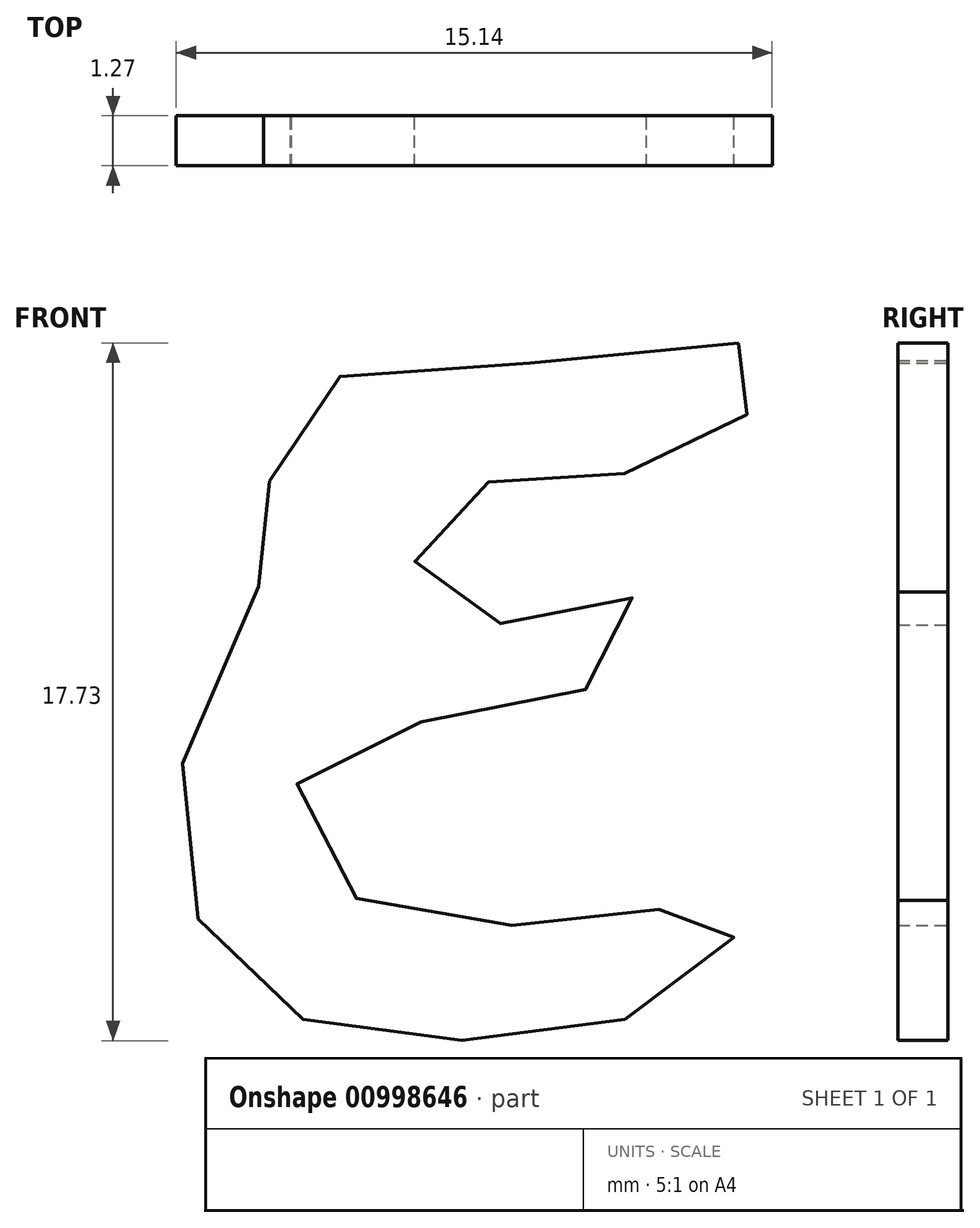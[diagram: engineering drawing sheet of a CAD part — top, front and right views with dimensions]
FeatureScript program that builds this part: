
annotation { "Feature Type Name" : "Feature", "Feature Type Description" : "" }
export const myFeature = defineFeature(function(context is Context, id is Id, definition is map)
    precondition{}
    {
        {
            var Q0;
            Q0=qCreatedBy(makeId("Front.planeOp"),FACE);
            var sketch = newSketch(context, id + "F0", { "sketchPlane" : qUnion([Q0])});
            skFitSpline(sketch, "E0", {"points": [v(-47.24, 22.97) * mm, v(-49.1, 22.78) * mm, v(-50.85, 22.6) * mm, v(-52.7, 22.46) * mm, v(-54.47, 22.52) * mm, v(-55.92, 22.46) * mm, v(-57.23, 22.17) * mm, v(-58.3, 21.53) * mm, v(-58.97, 20.74) * mm, v(-59.28, 20.08) * mm, v(-59.26, 19.68) * mm, v(-59.1, 19.4) * mm, v(-58.93, 19.24) * mm, v(-58.76, 19.07) * mm, v(-58.63, 18.78) * mm, v(-58.66, 18.35) * mm, v(-59.13, 17.31) * mm, v(-59.72, 16.2) * mm, v(-60.3, 14.91) * mm, v(-61, 13.4) * mm, v(-61.47, 11.75) * mm, v(-61.5, 10.6) * mm, v(-61.37, 9.66) * mm, v(-61.16, 8.8) * mm, v(-60.75, 7.95) * mm, v(-60.26, 7.24) * mm, v(-59.7, 6.62) * mm, v(-59.03, 6.11) * mm, v(-57.89, 5.65) * mm, v(-56.9, 5.43) * mm, v(-55.73, 5.29) * mm, v(-54.7, 5.26) * mm, v(-53.61, 5.24) * mm, v(-52.33, 5.34) * mm, v(-51.43, 5.48) * mm, v(-50.3, 5.72) * mm, v(-49.27, 6.1) * mm, v(-48.35, 6.6) * mm, v(-47.74, 7.17) * mm, v(-47.42, 7.65) * mm, v(-47.34, 8.01) * mm, v(-47.44, 8.4) * mm, v(-47.62, 8.6) * mm, v(-47.82, 8.73) * mm, v(-48.06, 8.8) * mm, v(-48.5, 8.75) * mm, v(-49.24, 8.58) * mm, v(-49.94, 8.44) * mm, v(-50.7, 8.35) * mm, v(-51.63, 8.26) * mm, v(-52.8, 8.18) * mm, v(-53.84, 8.18) * mm, v(-54.87, 8.24) * mm, v(-55.9, 8.46) * mm, v(-56.93, 8.84) * mm, v(-57.83, 9.4) * mm, v(-58.28, 10.02) * mm, v(-58.56, 10.66) * mm, v(-58.52, 11.53) * mm, v(-58.24, 12.23) * mm, v(-57.75, 12.82) * mm, v(-56.92, 13.12) * mm, v(-55.78, 13.29) * mm, v(-54.62, 13.4) * mm, v(-53.33, 13.56) * mm, v(-52.21, 13.83) * mm, v(-51.18, 14.13) * mm, v(-50.3, 14.58) * mm, v(-49.86, 15) * mm, v(-49.6, 15.59) * mm, v(-49.62, 16.08) * mm, v(-49.94, 16.5) * mm, v(-50.45, 16.63) * mm, v(-51.11, 16.48) * mm, v(-51.86, 16.2) * mm, v(-52.77, 15.94) * mm, v(-53.75, 15.8) * mm, v(-54.44, 15.94) * mm, v(-54.95, 16.21) * mm, v(-55.32, 16.63) * mm, v(-55.46, 17.14) * mm, v(-55.4, 17.68) * mm, v(-55.17, 18.24) * mm, v(-54.9, 18.63) * mm, v(-54.52, 19) * mm, v(-54.1, 19.27) * mm, v(-53.46, 19.46) * mm, v(-52.57, 19.57) * mm, v(-51.73, 19.58) * mm, v(-50.9, 19.6) * mm, v(-50.34, 19.63) * mm, v(-49.69, 19.72) * mm, v(-49.02, 19.92) * mm, v(-48.1, 20.33) * mm, v(-47.47, 20.78) * mm, v(-46.9, 21.26) * mm, v(-46.49, 21.74) * mm, v(-46.38, 22.1) * mm, v(-46.4, 22.4) * mm, v(-46.55, 22.66) * mm, v(-46.82, 22.88) * mm, v(-47.24, 22.97) * mm]});
            skLineSegment(sketch, "E1.bottom", {"start": v(-120.44, 77.9) * mm, "end": v(12.9, 77.9) * mm});
            skLineSegment(sketch, "E1.top", {"start": v(-120.44, -131.65) * mm, "end": v(12.9, -131.65) * mm});
            skLineSegment(sketch, "E1.left", {"start": v(-120.44, 77.9) * mm, "end": v(-120.44, -131.65) * mm});
            skLineSegment(sketch, "E1.right", {"start": v(12.9, 77.9) * mm, "end": v(12.9, -131.65) * mm});
            skLineSegment(sketch, "E2", {"start": v(-53.77, 77.9) * mm, "end": v(-53.77, -131.65) * mm, "construction": true});
            skLineSegment(sketch, "E3", {"start": v(-120.44, 14.4) * mm, "end": v(12.9, 14.4) * mm, "construction": true});
            skLineSegment(sketch, "E4", {"start": v(-61.7, 14.4) * mm, "end": v(-63.46, 14.4) * mm, "construction": true});
            skLineSegment(sketch, "E5", {"start": v(-53.77, 23.92) * mm, "end": v(-53.77, 28.89) * mm, "construction": true});
            skLineSegment(sketch, "E6", {"start": v(-53.77, 28.89) * mm, "end": v(-53.93, 28.89) * mm, "construction": true});
            skPoint(sketch, "E7.orphan", {"position": v(-61.7, 23.92) * mm});
            skPoint(sketch, "E8.orphan", {"position": v(-61.7, 4.87) * mm});
            skPoint(sketch, "E9.right.start.orphan", {"position": v(-45.83, 23.92) * mm});
            skFitSpline(sketch, "E10.0", {"points": [v(-46.96, 23) * mm, v(-47.22, 23.02) * mm, v(-47.62, 23) * mm, v(-48.11, 22.95) * mm, v(-48.65, 22.88) * mm, v(-49.36, 22.8) * mm, v(-49.98, 22.74) * mm, v(-50.57, 22.68) * mm, v(-51.18, 22.62) * mm, v(-51.82, 22.55) * mm, v(-52.48, 22.51) * mm, v(-53.12, 22.5) * mm, v(-53.92, 22.55) * mm, v(-54.82, 22.58) * mm, v(-55.67, 22.54) * mm, v(-56.5, 22.44) * mm, v(-57.3, 22.23) * mm, v(-57.9, 21.9) * mm, v(-58.32, 21.59) * mm, v(-58.69, 21.24) * mm, v(-58.97, 20.85) * mm, v(-59.2, 20.46) * mm, v(-59.32, 20.18) * mm, v(-59.36, 19.92) * mm, v(-59.33, 19.7) * mm, v(-59.24, 19.49) * mm, v(-59.11, 19.32) * mm, v(-58.97, 19.22) * mm, v(-58.85, 19.11) * mm, v(-58.75, 18.98) * mm, v(-58.68, 18.8) * mm, v(-58.65, 18.6) * mm, v(-58.7, 18.37) * mm, v(-58.81, 18.05) * mm, v(-58.98, 17.7) * mm, v(-59.18, 17.33) * mm, v(-59.37, 16.98) * mm, v(-59.56, 16.64) * mm, v(-59.8, 16.17) * mm, v(-60.02, 15.66) * mm, v(-60.25, 15.14) * mm, v(-60.5, 14.61) * mm, v(-60.77, 14.07) * mm, v(-61.02, 13.5) * mm, v(-61.25, 12.9) * mm, v(-61.43, 12.28) * mm, v(-61.53, 11.7) * mm, v(-61.58, 11.16) * mm, v(-61.56, 10.56) * mm, v(-61.48, 9.98) * mm, v(-61.4, 9.54) * mm, v(-61.33, 9.2) * mm, v(-61.25, 8.88) * mm, v(-61.09, 8.45) * mm, v(-60.81, 7.93) * mm, v(-60.51, 7.47) * mm, v(-60.24, 7.13) * mm, v(-60.02, 6.88) * mm, v(-59.8, 6.65) * mm, v(-59.56, 6.43) * mm, v(-59.31, 6.23) * mm, v(-59.02, 6.04) * mm, v(-58.66, 5.87) * mm, v(-58.28, 5.72) * mm, v(-57.9, 5.6) * mm, v(-57.55, 5.5) * mm, v(-57.21, 5.43) * mm, v(-56.74, 5.35) * mm, v(-56.22, 5.28) * mm, v(-55.7, 5.23) * mm, v(-55.21, 5.2) * mm, v(-54.75, 5.2) * mm, v(-54.27, 5.2) * mm, v(-53.9, 5.19) * mm, v(-53.51, 5.2) * mm, v(-52.96, 5.22) * mm, v(-52.4, 5.27) * mm, v(-51.96, 5.33) * mm, v(-51.64, 5.39) * mm, v(-51.3, 5.45) * mm, v(-50.93, 5.52) * mm, v(-50.54, 5.6) * mm, v(-50.04, 5.74) * mm, v(-49.58, 5.91) * mm, v(-49.13, 6.11) * mm, v(-48.8, 6.28) * mm, v(-48.48, 6.46) * mm, v(-48.1, 6.73) * mm, v(-47.7, 7.1) * mm, v(-47.36, 7.57) * mm, v(-47.27, 7.94) * mm, v(-47.33, 8.26) * mm, v(-47.42, 8.47) * mm, v(-47.55, 8.62) * mm, v(-47.7, 8.73) * mm, v(-47.86, 8.81) * mm, v(-48.04, 8.86) * mm, v(-48.26, 8.85) * mm, v(-48.52, 8.8) * mm, v(-48.82, 8.73) * mm, v(-49.14, 8.65) * mm, v(-49.44, 8.58) * mm, v(-49.73, 8.53) * mm, v(-50.02, 8.48) * mm, v(-50.42, 8.43) * mm, v(-50.94, 8.37) * mm, v(-51.63, 8.3) * mm, v(-52.28, 8.25) * mm, v(-52.79, 8.23) * mm, v(-53.28, 8.22) * mm, v(-53.86, 8.23) * mm, v(-54.58, 8.24) * mm, v(-55.3, 8.34) * mm, v(-55.88, 8.5) * mm, v(-56.34, 8.65) * mm, v(-56.68, 8.79) * mm, v(-57.02, 8.94) * mm, v(-57.36, 9.12) * mm, v(-57.66, 9.31) * mm, v(-57.9, 9.53) * mm, v(-58.08, 9.77) * mm, v(-58.23, 10.03) * mm, v(-58.38, 10.29) * mm, v(-58.49, 10.55) * mm, v(-58.54, 10.85) * mm, v(-58.53, 11.18) * mm, v(-58.48, 11.5) * mm, v(-58.39, 11.8) * mm, v(-58.27, 12.07) * mm, v(-58.12, 12.34) * mm, v(-57.94, 12.6) * mm, v(-57.73, 12.8) * mm, v(-57.46, 12.93) * mm, v(-57.14, 13.02) * mm, v(-56.78, 13.1) * mm, v(-56.28, 13.18) * mm, v(-55.65, 13.26) * mm, v(-55.03, 13.3) * mm, v(-54.5, 13.35) * mm, v(-53.97, 13.4) * mm, v(-53.28, 13.5) * mm, v(-52.67, 13.66) * mm, v(-52.2, 13.78) * mm, v(-51.72, 13.9) * mm, v(-51.24, 14.04) * mm, v(-50.78, 14.25) * mm, v(-50.47, 14.41) * mm, v(-50.2, 14.59) * mm, v(-49.97, 14.76) * mm, v(-49.8, 14.97) * mm, v(-49.65, 15.24) * mm, v(-49.55, 15.53) * mm, v(-49.51, 15.8) * mm, v(-49.54, 16.05) * mm, v(-49.66, 16.3) * mm, v(-49.85, 16.51) * mm, v(-50.1, 16.64) * mm, v(-50.37, 16.7) * mm, v(-50.66, 16.67) * mm, v(-50.95, 16.6) * mm, v(-51.34, 16.45) * mm, v(-51.73, 16.3) * mm, v(-52.14, 16.16) * mm, v(-52.47, 16.06) * mm, v(-52.82, 15.98) * mm, v(-53.17, 15.9) * mm, v(-53.52, 15.85) * mm, v(-53.85, 15.85) * mm, v(-54.14, 15.9) * mm, v(-54.4, 15.98) * mm, v(-54.65, 16.08) * mm, v(-54.87, 16.21) * mm, v(-55.08, 16.38) * mm, v(-55.24, 16.58) * mm, v(-55.35, 16.8) * mm, v(-55.4, 17.04) * mm, v(-55.42, 17.3) * mm, v(-55.4, 17.54) * mm, v(-55.33, 17.8) * mm, v(-55.21, 18.06) * mm, v(-55.09, 18.29) * mm, v(-54.96, 18.48) * mm, v(-54.8, 18.66) * mm, v(-54.62, 18.84) * mm, v(-54.43, 19) * mm, v(-54.24, 19.15) * mm, v(-54.02, 19.26) * mm, v(-53.75, 19.35) * mm, v(-53.46, 19.42) * mm, v(-53.13, 19.47) * mm, v(-52.8, 19.5) * mm, v(-52.35, 19.53) * mm, v(-51.93, 19.52) * mm, v(-51.49, 19.53) * mm, v(-51.16, 19.54) * mm, v(-50.85, 19.56) * mm, v(-50.6, 19.56) * mm, v(-50.33, 19.58) * mm, v(-50.05, 19.6) * mm, v(-49.75, 19.65) * mm, v(-49.47, 19.71) * mm, v(-49.2, 19.8) * mm, v(-48.79, 19.95) * mm, v(-48.31, 20.15) * mm, v(-47.92, 20.38) * mm, v(-47.66, 20.56) * mm, v(-47.43, 20.75) * mm, v(-47.1, 21) * mm, v(-46.8, 21.28) * mm, v(-46.53, 21.57) * mm, v(-46.4, 21.8) * mm, v(-46.33, 22.01) * mm, v(-46.31, 22.3) * mm, v(-46.4, 22.56) * mm, v(-46.58, 22.78) * mm, v(-46.76, 22.92) * mm, v(-46.96, 23) * mm, v(-47.22, 23.02) * mm, v(-47.62, 23) * mm, v(-46.96, 23) * mm]});
            skSolve(sketch);
        }
        {
            var Q0;
            Q0=makeQuery(id+"F0.imprint","IMPRINT",FACE,{"disambiguationData":[TD([[makeQuery(id+"F0.imprint","IMPRINT",EDGE,{"derivedFrom":sQuery(id+"F0.wireOp",EDGE,"E0")}),1.0]])]});
            extrude(context, id + "F1", {"entities" : qUnion([Q0]), "depth" : 1.27 * mm, "offsetDistance" : 25.4 * mm});
        }
    });
